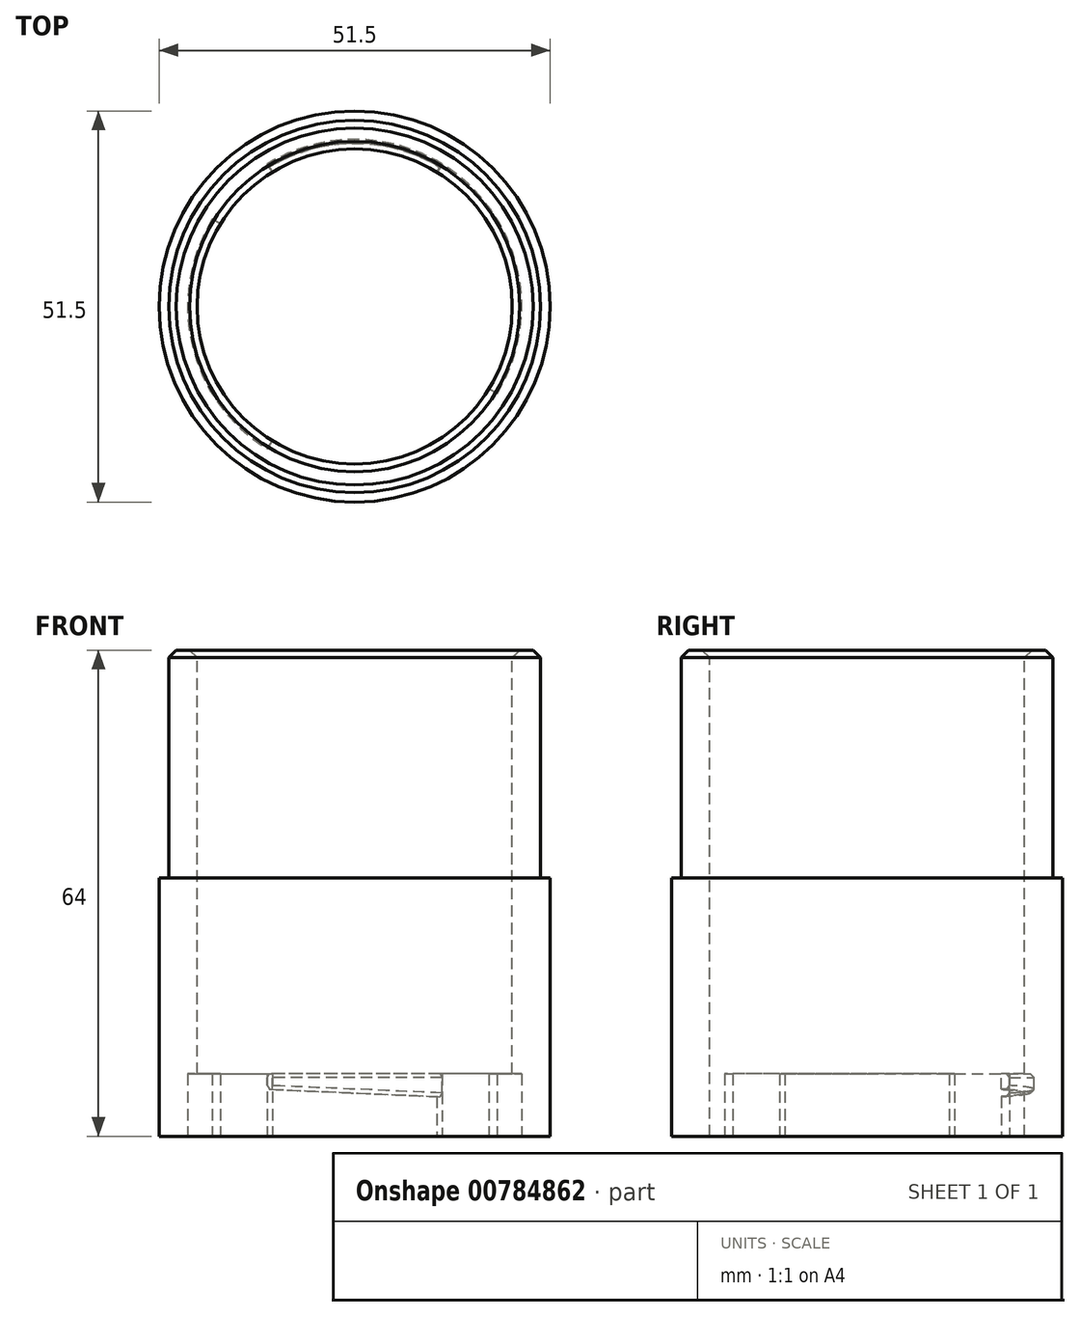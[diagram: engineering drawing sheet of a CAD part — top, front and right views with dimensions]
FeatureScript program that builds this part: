
annotation { "Feature Type Name" : "Feature", "Feature Type Description" : "" }
export const myFeature = defineFeature(function(context is Context, id is Id, definition is map)
    precondition{}
    {
        {
            var Q0;
            Q0=qCreatedBy(makeId("Top.planeOp"),FACE);
            var sketch = newSketch(context, id + "F0", { "sketchPlane" : qUnion([Q0])});
            skCircle(sketch, "E0", {"center": v(0, 0) * mm, "radius": 20.75 * mm});
            skCircle(sketch, "E1", {"center": v(0, 0) * mm, "radius": 18.75 * mm});
            skSolve(sketch);
        }
        {
            var Q0;
            Q0=makeQuery(id+"F0.imprint","IMPRINT",FACE,{"disambiguationData":[TD([[makeQuery(id+"F0.imprint","IMPRINT",EDGE,{"derivedFrom":sQuery(id+"F0.wireOp",EDGE,"E0")}),1.0]])]});
            extrude(context, id + "F1", {"entities" : qUnion([Q0]), "depth" : 34 * mm});
        }
        {
            var Q0;
            Q0=makeQuery(id+"F1.opExtrude","CAP_FACE",FACE,{"disambiguationData":[OSD([sQuery(id+"F0.wireOp",EDGE,"E0"),sQuery(id+"F0.wireOp",EDGE,"E1")])],"isStart":false});
            cPlane(context, id + "F2", {"entities" : qUnion([Q0]), "cplaneType" : CPlaneType.OFFSET, "offset" : 25.8 * mm, "oppositeDirection" : true, "width" : 150 * mm, "height" : 150 * mm});
        }
        {
            var Q0;
            Q0=qCreatedBy(id+"F2.planeOp",FACE);
            var sketch = newSketch(context, id + "F3", { "sketchPlane" : qUnion([Q0])});
            skCircle(sketch, "E2.0", {"center": v(0, 0) * mm, "radius": 20.75 * mm});
            skCircle(sketch, "E3", {"center": v(0, 0) * mm, "radius": 22 * mm});
            skLineSegment(sketch, "E4", {"start": v(-11.5, 18.75) * mm, "end": v(11.5, -18.75) * mm});
            skLineSegment(sketch, "E5", {"start": v(-11.5, -18.75) * mm, "end": v(11.5, 18.75) * mm});
            skLineSegment(sketch, "E6", {"start": v(-11.5, 18.75) * mm, "end": v(0, 21.22) * mm, "construction": true});
            skLineSegment(sketch, "E7", {"start": v(0, 21.22) * mm, "end": v(11.5, 18.75) * mm, "construction": true});
            skSolve(sketch);
        }
        {
            var Q0;
            {var subQ0=sQuery(id+"F3.wireOp",EDGE,"E4");var subQ1=sQuery(id+"F3.wireOp",EDGE,"E2.0");var subQ2=makeQuery(id+"F3.imprint","INTERSECT",VERTEX,{"disambiguationData":[OD(0.0)],"derivedFrom":[subQ1,subQ0]});Q0=makeQuery(id+"F3.imprint","IMPRINT",FACE,{"disambiguationData":[TD([[makeQuery(id+"F3.imprint","IMPRINT",EDGE,{"disambiguationData":[TD([[subQ2,1.0]])],"derivedFrom":subQ1}),-1.0]])]});}
            var Q1;
            {var subQ0=sQuery(id+"F3.wireOp",EDGE,"E5");var subQ1=sQuery(id+"F3.wireOp",EDGE,"E2.0");var subQ2=makeQuery(id+"F3.imprint","INTERSECT",VERTEX,{"disambiguationData":[OD(1.0)],"derivedFrom":[subQ1,subQ0]});Q1=makeQuery(id+"F3.imprint","IMPRINT",FACE,{"disambiguationData":[TD([[makeQuery(id+"F3.imprint","IMPRINT",EDGE,{"disambiguationData":[TD([[subQ2,-1.0]])],"derivedFrom":subQ1}),-1.0]])]});}
            extrude(context, id + "F4", {"entities" : qUnion([Q0, Q1]), "operationType" : NewBodyOperationType.ADD, "oppositeDirection" : true, "depth" : 3 * mm, "offsetDistance" : 25 * mm});
        }
        {
            var Q0;
            Q0=qCreatedBy(makeId("Front.planeOp"),FACE);
            cPlane(context, id + "F5", {"entities" : qUnion([Q0]), "cplaneType" : CPlaneType.OFFSET, "offset" : 25 * mm, "width" : 150 * mm, "height" : 150 * mm});
        }
        {
            var Q0;
            Q0=qCreatedBy(id+"F5.planeOp",FACE);
            var sketch = newSketch(context, id + "F6", { "sketchPlane" : qUnion([Q0])});
            skLineSegment(sketch, "E8.0.0", {"start": v(11.5, 8.2) * mm, "end": v(-11.5, 8.2) * mm});
            skLineSegment(sketch, "E8.0.1", {"start": v(-11.5, 8.2) * mm, "end": v(-11.5, 5.2) * mm});
            skLineSegment(sketch, "E8.0.2", {"start": v(-11.5, 5.2) * mm, "end": v(11.5, 5.2) * mm});
            skLineSegment(sketch, "E8.0.3", {"start": v(11.5, 5.2) * mm, "end": v(11.5, 8.2) * mm});
            skLineSegment(sketch, "E9", {"start": v(11.5, 6.2) * mm, "end": v(-11.5, 5.2) * mm});
            skSolve(sketch);
        }
        {
            var Q0;
            {var subQ0=sQuery(id+"F6.wireOp",EDGE,"E8.0.2");Q0=makeQuery(id+"F6.imprint","IMPRINT",FACE,{"disambiguationData":[TD([[makeQuery(id+"F6.imprint","IMPRINT",EDGE,{"derivedFrom":subQ0}),1.0]])]});}
            var Q1;
            Q1=makeQuery(id+"F1.opExtrude","SWEPT_FACE",FACE,{"disambiguationData":[OSD([sQuery(id+"F0.wireOp",EDGE,"E0")])]});
            extrude(context, id + "F7", {"entities" : qUnion([Q0]), "operationType" : NewBodyOperationType.REMOVE, "endBound" : BoundingType.UP_TO_SURFACE, "oppositeDirection" : true, "endBoundEntityFace" : qUnion([Q1]), "depth" : 25 * mm});
        }
        {
            var Q0;
            Q0=qCreatedBy(makeId("Front.planeOp"),FACE);
            cPlane(context, id + "F8", {"entities" : qUnion([Q0]), "cplaneType" : CPlaneType.OFFSET, "offset" : 25 * mm, "oppositeDirection" : true, "width" : 150 * mm, "height" : 150 * mm});
        }
        {
            var Q0;
            Q0=qCreatedBy(id+"F8.planeOp",FACE);
            var sketch = newSketch(context, id + "F9", { "sketchPlane" : qUnion([Q0])});
            skLineSegment(sketch, "E10.0.0", {"start": v(-11.5, 8.2) * mm, "end": v(11.5, 8.2) * mm});
            skLineSegment(sketch, "E10.0.1", {"start": v(11.5, 8.2) * mm, "end": v(11.5, 5.2) * mm});
            skLineSegment(sketch, "E10.0.2", {"start": v(11.5, 5.2) * mm, "end": v(-11.5, 5.2) * mm});
            skLineSegment(sketch, "E10.0.3", {"start": v(-11.5, 5.2) * mm, "end": v(-11.5, 8.2) * mm});
            skLineSegment(sketch, "E11", {"start": v(11.5, 5.2) * mm, "end": v(-11.5, 6.2) * mm});
            skSolve(sketch);
        }
        {
            var Q0;
            {var subQ0=sQuery(id+"F9.wireOp",EDGE,"E10.0.2");Q0=makeQuery(id+"F9.imprint","IMPRINT",FACE,{"disambiguationData":[TD([[makeQuery(id+"F9.imprint","IMPRINT",EDGE,{"derivedFrom":subQ0}),-1.0]])]});}
            var Q1;
            Q1=makeQuery(id+"F7.boolean.opBoolean","MERGE",FACE,{"derivedFrom":[makeQuery(id+"F1.opExtrude","SWEPT_FACE",FACE,{"disambiguationData":[OSD([sQuery(id+"F0.wireOp",EDGE,"E0")])]})],"fromTools":[makeQuery(id+"F7.opExtrude","CAP_FACE",FACE,{"disambiguationData":[OSD([sQuery(id+"F6.wireOp",EDGE,"E8.0.2"),sQuery(id+"F6.wireOp",EDGE,"E8.0.3"),sQuery(id+"F6.wireOp",EDGE,"E9")])],"isStart":false})]});
            extrude(context, id + "F10", {"entities" : qUnion([Q0]), "operationType" : NewBodyOperationType.REMOVE, "endBound" : BoundingType.UP_TO_SURFACE, "endBoundEntityFace" : qUnion([Q1]), "depth" : 25 * mm});
        }
        {
            var Q0;
            Q0=makeQuery(id+"F1.opExtrude","CAP_FACE",FACE,{"disambiguationData":[OSD([sQuery(id+"F0.wireOp",EDGE,"E0"),sQuery(id+"F0.wireOp",EDGE,"E1")])],"isStart":true});
            var sketch = newSketch(context, id + "F11", { "sketchPlane" : qUnion([Q0])});
            skCircle(sketch, "E12", {"center": v(0, 0) * mm, "radius": 24.25 * mm});
            skSolve(sketch);
        }
        {
            var Q0;
            Q0=makeQuery(id+"F11.imprint","IMPRINT",FACE,{"disambiguationData":[TD([[makeQuery(id+"F11.imprint","IMPRINT",EDGE,{"derivedFrom":sQuery(id+"F11.wireOp",EDGE,"E12")}),1.0]])]});
            var Q1;
            Q1=makeQuery(id+"F11.imprint","IMPRINT",FACE,{"disambiguationData":[TD([[makeQuery(id+"F11.imprint","IMPRINT",EDGE,{"derivedFrom":makeQuery(id+"F1.opExtrude","CAP_EDGE",EDGE,{"disambiguationData":[OSD([sQuery(id+"F0.wireOp",EDGE,"E0")])],"isStart":true})}),-1.0]])]});
            extrude(context, id + "F12", {"entities" : qUnion([Q0, Q1]), "operationType" : NewBodyOperationType.ADD, "depth" : 3 * mm});
        }
        {
            var Q0;
            Q0=makeQuery(id+"F12.opExtrude","CAP_FACE",FACE,{"disambiguationData":[OSD([sQuery(id+"F0.wireOp",EDGE,"E1"),sQuery(id+"F11.wireOp",EDGE,"E12")])],"isStart":false});
            var sketch = newSketch(context, id + "F13", { "sketchPlane" : qUnion([Q0])});
            skCircle(sketch, "E13.0", {"center": v(0, 0) * mm, "radius": 20.75 * mm});
            skCircle(sketch, "E14", {"center": v(0, 0) * mm, "radius": 16.75 * mm});
            skCircle(sketch, "E15.0", {"center": v(0, 0) * mm, "radius": 18.75 * mm});
            skSolve(sketch);
        }
        {
            var Q0;
            Q0=makeQuery(id+"F13.imprint","IMPRINT",FACE,{"disambiguationData":[TD([[makeQuery(id+"F13.imprint","IMPRINT",EDGE,{"derivedFrom":sQuery(id+"F13.wireOp",EDGE,"E14")}),-1.0]])]});
            extrude(context, id + "F14", {"entities" : qUnion([Q0]), "operationType" : NewBodyOperationType.ADD, "oppositeDirection" : true, "depth" : 3 * mm});
        }
        {
            var Q0;
            Q0=makeQuery(id+"F13.imprint","IMPRINT",FACE,{"disambiguationData":[TD([[makeQuery(id+"F13.imprint","IMPRINT",EDGE,{"derivedFrom":sQuery(id+"F13.wireOp",EDGE,"E13.0")}),1.0]])]});
            extrude(context, id + "F15", {"entities" : qUnion([Q0]), "operationType" : NewBodyOperationType.ADD, "depth" : 35 * mm});
        }
        {
            var Q0;
            Q0=makeQuery(id+"F1.opExtrude","CAP_EDGE",EDGE,{"disambiguationData":[OSD([sQuery(id+"F0.wireOp",EDGE,"E0")])],"isStart":false});
            var Q1;
            Q1=makeQuery(id+"F1.opExtrude","CAP_EDGE",EDGE,{"disambiguationData":[OSD([sQuery(id+"F0.wireOp",EDGE,"E1")])],"isStart":false});
            var Q2;
            {var subQ0=sQuery(id+"F3.wireOp",EDGE,"E3");Q2=makeQuery(id+"F4.opExtrude","CAP_EDGE",EDGE,{"disambiguationData":[OSD([subQ0]),TDD([makeQuery(id+"F3.imprint","IMPRINT",EDGE,{"disambiguationData":[TD([[makeQuery(id+"F3.imprint","INTERSECT",VERTEX,{"disambiguationData":[OD(1.0)],"derivedFrom":[subQ0,sQuery(id+"F3.wireOp",EDGE,"E4")]}),1.0]])],"derivedFrom":subQ0})])],"isStart":true});}
            var Q3;
            {var subQ0=sQuery(id+"F3.wireOp",EDGE,"E3");Q3=makeQuery(id+"F7.boolean.opBoolean","INTERSECT",EDGE,{"derivedFrom":[makeQuery(id+"F4.opExtrude","SWEPT_FACE",FACE,{"disambiguationData":[OSD([subQ0]),TDD([makeQuery(id+"F3.imprint","IMPRINT",EDGE,{"disambiguationData":[TD([[makeQuery(id+"F3.imprint","INTERSECT",VERTEX,{"disambiguationData":[OD(1.0)],"derivedFrom":[subQ0,sQuery(id+"F3.wireOp",EDGE,"E4")]}),1.0]])],"derivedFrom":subQ0})])]}),makeQuery(id+"F7.opExtrude","SWEPT_FACE",FACE,{"disambiguationData":[OSD([sQuery(id+"F6.wireOp",EDGE,"E9")])]})]});}
            var Q4;
            {var subQ0=sQuery(id+"F3.wireOp",EDGE,"E3");Q4=makeQuery(id+"F4.opExtrude","CAP_EDGE",EDGE,{"disambiguationData":[OSD([subQ0]),TDD([makeQuery(id+"F3.imprint","IMPRINT",EDGE,{"disambiguationData":[TD([[makeQuery(id+"F3.imprint","INTERSECT",VERTEX,{"disambiguationData":[OD(0.0)],"derivedFrom":[subQ0,sQuery(id+"F3.wireOp",EDGE,"E4")]}),1.0]])],"derivedFrom":subQ0})])],"isStart":true});}
            var Q5;
            {var subQ0=sQuery(id+"F3.wireOp",EDGE,"E3");Q5=makeQuery(id+"F10.boolean.opBoolean","INTERSECT",EDGE,{"derivedFrom":[makeQuery(id+"F4.opExtrude","SWEPT_FACE",FACE,{"disambiguationData":[OSD([subQ0]),TDD([makeQuery(id+"F3.imprint","IMPRINT",EDGE,{"disambiguationData":[TD([[makeQuery(id+"F3.imprint","INTERSECT",VERTEX,{"disambiguationData":[OD(0.0)],"derivedFrom":[subQ0,sQuery(id+"F3.wireOp",EDGE,"E4")]}),1.0]])],"derivedFrom":subQ0})])]}),makeQuery(id+"F10.opExtrude","SWEPT_FACE",FACE,{"disambiguationData":[OSD([sQuery(id+"F9.wireOp",EDGE,"E11")])]})]});}
            var Q6;
            Q6=makeQuery(id+"F1.opExtrude","CAP_EDGE",EDGE,{"disambiguationData":[OSD([sQuery(id+"F0.wireOp",EDGE,"E0")])],"isStart":true});
            chamfer(context, id + "F16", {"entities" : qUnion([Q0, Q1, Q2, Q3, Q4, Q5, Q6]), "width" : 0.5 * mm, "tangentPropagation" : true});
        }
        {
            var Q0;
            Q0=makeQuery(id+"F14.opExtrude","CAP_EDGE",EDGE,{"disambiguationData":[OSD([sQuery(id+"F13.wireOp",EDGE,"E14")])],"isStart":true});
            var Q1;
            Q1=makeQuery(id+"F14.opExtrude","CAP_EDGE",EDGE,{"disambiguationData":[OSD([sQuery(id+"F13.wireOp",EDGE,"E14")])],"isStart":false});
            var Q2;
            Q2=makeQuery(id+"F15.opExtrude","CAP_EDGE",EDGE,{"disambiguationData":[OSD([sQuery(id+"F13.wireOp",EDGE,"E13.0")])],"isStart":true});
            var Q3;
            Q3=makeQuery(id+"F12.opExtrude","CAP_EDGE",EDGE,{"disambiguationData":[OSD([sQuery(id+"F11.wireOp",EDGE,"E12")])],"isStart":false});
            var Q4;
            Q4=makeQuery(id+"F12.opExtrude","CAP_EDGE",EDGE,{"disambiguationData":[OSD([sQuery(id+"F11.wireOp",EDGE,"E12")])],"isStart":true});
            fillet(context, id + "F17", {"entities" : qUnion([Q0, Q1, Q2, Q3, Q4]), "radius" : 1.5 * mm, "tangentPropagation" : true, "allowEdgeOverflow" : false});
        }
        {
            var Q0;
            Q0=makeQuery(id+"F1.opExtrude","CAP_FACE",FACE,{"disambiguationData":[OSD([sQuery(id+"F0.wireOp",EDGE,"E0"),sQuery(id+"F0.wireOp",EDGE,"E1")])],"isStart":false});
            var sketch = newSketch(context, id + "F18", { "sketchPlane" : qUnion([Q0])});
            skCircle(sketch, "E16", {"center": v(0, 0) * mm, "radius": 24.75 * mm});
            skCircle(sketch, "E17.0", {"center": v(0, 0) * mm, "radius": 20.75 * mm});
            skSolve(sketch);
        }
        {
            var Q0;
            Q0=makeQuery(id+"F18.imprint","IMPRINT",FACE,{"disambiguationData":[TD([[makeQuery(id+"F18.imprint","IMPRINT",EDGE,{"derivedFrom":sQuery(id+"F18.wireOp",EDGE,"E16")}),1.0]])]});
            var Q1;
            Q1=makeQuery(id+"F12.opExtrude","CAP_FACE",FACE,{"disambiguationData":[OSD([sQuery(id+"F0.wireOp",EDGE,"E1"),sQuery(id+"F11.wireOp",EDGE,"E12")])],"isStart":true});
            extrude(context, id + "F19", {"entities" : qUnion([Q0]), "endBound" : BoundingType.UP_TO_SURFACE, "oppositeDirection" : true, "endBoundEntityFace" : qUnion([Q1]), "depth" : 35 * mm});
        }
        {
            var Q0;
            Q0=makeQuery(id+"F1.opExtrude","SWEPT_BODY",BODY,{"disambiguationData":[OSD([sQuery(id+"F0.wireOp",EDGE,"E0"),sQuery(id+"F0.wireOp",EDGE,"E1")])]});
            var Q1;
            Q1=makeQuery(id+"F19.opExtrude","SWEPT_BODY",BODY,{"disambiguationData":[OSD([sQuery(id+"F18.wireOp",EDGE,"E16"),sQuery(id+"F18.wireOp",EDGE,"E17.0")])]});
            booleanBodies(context, id + "F20", {"operationType" : BooleanOperationType.SUBTRACTION, "tools" : qUnion([Q0]), "targets" : qUnion([Q1])});
        }
        {
            var Q0;
            Q0=makeQuery(id+"F19.opExtrude","CAP_FACE",FACE,{"disambiguationData":[OSD([sQuery(id+"F18.wireOp",EDGE,"E16"),sQuery(id+"F18.wireOp",EDGE,"E17.0")])],"isStart":false});
            var sketch = newSketch(context, id + "F21", { "sketchPlane" : qUnion([Q0])});
            skLineSegment(sketch, "E18.0.0", {"start": v(-11.23, 18.32) * mm, "end": v(-10.85, 17.69) * mm});
            skLineSegment(sketch, "E18.0.2", {"start": v(-10.85, 17.69) * mm, "end": v(-11.24, 18.33) * mm});
            skLineSegment(sketch, "E18.0.3", {"start": v(-11.5, 18.75) * mm, "end": v(-11.24, 18.33) * mm});
            skFitSpline(sketch, "E18.0.5", {"points": [v(-11.5, 18.76) * mm, v(-11.41, 18.61) * mm, v(-11.32, 18.47) * mm, v(-11.23, 18.32) * mm]});
            skLineSegment(sketch, "E19.0.0", {"start": v(11.23, -18.32) * mm, "end": v(10.85, -17.69) * mm});
            skLineSegment(sketch, "E19.0.2", {"start": v(10.85, -17.69) * mm, "end": v(11.24, -18.33) * mm});
            skLineSegment(sketch, "E19.0.3", {"start": v(11.24, -18.33) * mm, "end": v(11.5, -18.75) * mm});
            skFitSpline(sketch, "E19.0.5", {"points": [v(11.5, -18.76) * mm, v(11.41, -18.61) * mm, v(11.32, -18.47) * mm, v(11.23, -18.32) * mm]});
            skCircle(sketch, "E20", {"center": v(0, 0) * mm, "radius": 20.75 * mm});
            skCircle(sketch, "E21", {"center": v(0, 0) * mm, "radius": 22 * mm});
            skLineSegment(sketch, "E22", {"start": v(18.76, 11.5) * mm, "end": v(0, 0) * mm});
            skLineSegment(sketch, "E23", {"start": v(0, 0) * mm, "end": v(-18.76, -11.5) * mm});
            skSolve(sketch);
        }
        {
            var Q0;
            {var subQ0=sQuery(id+"F21.wireOp",EDGE,"E19.0.5");var subQ3=makeQuery(id+"F21.imprint","IMPRINT",VERTEX,{"derivedFrom":subQ0});Q0=makeQuery(id+"F21.imprint","IMPRINT",FACE,{"disambiguationData":[TD([[makeQuery(id+"F21.imprint","IMPRINT",EDGE,{"disambiguationData":[TD([[subQ3,1.0]])],"derivedFrom":subQ0}),-1.0]])]});}
            var Q1;
            {var subQ0=sQuery(id+"F21.wireOp",EDGE,"E20");var subQ1=sQuery(id+"F21.wireOp",EDGE,"E19.0.2");var subQ2=makeQuery(id+"F21.imprint","INTERSECT",VERTEX,{"derivedFrom":[subQ1,subQ0]});Q1=makeQuery(id+"F21.imprint","IMPRINT",FACE,{"disambiguationData":[TD([[makeQuery(id+"F21.imprint","IMPRINT",EDGE,{"disambiguationData":[TD([[subQ2,-1.0]])],"derivedFrom":subQ0}),-1.0]])]});}
            var Q2;
            {var subQ1=sQuery(id+"F21.wireOp",EDGE,"E18.0.5");var subQ5=makeQuery(id+"F21.imprint","IMPRINT",VERTEX,{"derivedFrom":subQ1});Q2=makeQuery(id+"F21.imprint","IMPRINT",FACE,{"disambiguationData":[TD([[makeQuery(id+"F21.imprint","IMPRINT",EDGE,{"disambiguationData":[TD([[subQ5,1.0]])],"derivedFrom":subQ1}),-1.0]])]});}
            var Q3;
            {var subQ0=sQuery(id+"F21.wireOp",EDGE,"E20");var subQ1=sQuery(id+"F21.wireOp",EDGE,"E18.0.2");var subQ2=makeQuery(id+"F21.imprint","INTERSECT",VERTEX,{"derivedFrom":[subQ1,subQ0]});Q3=makeQuery(id+"F21.imprint","IMPRINT",FACE,{"disambiguationData":[TD([[makeQuery(id+"F21.imprint","IMPRINT",EDGE,{"disambiguationData":[TD([[subQ2,-1.0]])],"derivedFrom":subQ0}),-1.0]])]});}
            var Q4;
            {var subQ0=sQuery(id+"F3.wireOp",EDGE,"E5");var subQ1=sQuery(id+"F3.wireOp",EDGE,"E3");var subQ2=makeQuery(id+"F3.imprint","INTERSECT",VERTEX,{"disambiguationData":[OD(1.0)],"derivedFrom":[subQ1,subQ0]});var subQ3=sQuery(id+"F3.wireOp",EDGE,"E2.0");var subQ5=sQuery(id+"F3.wireOp",EDGE,"E4");var subQ6=makeQuery(id+"F3.imprint","INTERSECT",VERTEX,{"disambiguationData":[OD(0.0)],"derivedFrom":[subQ1,subQ5]});var subQ7=makeQuery(id+"F3.imprint","INTERSECT",VERTEX,{"disambiguationData":[OD(0.0)],"derivedFrom":[subQ3,subQ5]});Q4=makeQuery(id+"F20.opBoolean","COPY",FACE,{"derivedFrom":makeQuery(id+"F4.opExtrude","CAP_FACE",FACE,{"disambiguationData":[OSD([subQ3,subQ1,subQ5,subQ0]),TDD([makeQuery(id+"F3.imprint","IMPRINT",EDGE,{"disambiguationData":[TD([[subQ7,1.0]])],"derivedFrom":subQ3}),makeQuery(id+"F3.imprint","IMPRINT",EDGE,{"disambiguationData":[TD([[subQ6,1.0]])],"derivedFrom":subQ1}),makeQuery(id+"F3.imprint","IMPRINT",EDGE,{"disambiguationData":[TD([[subQ6,-1.0]])],"derivedFrom":subQ5}),makeQuery(id+"F3.imprint","IMPRINT",EDGE,{"disambiguationData":[TD([[subQ2,1.0]])],"derivedFrom":subQ0})])],"isStart":true})});}
            extrude(context, id + "F22", {"entities" : qUnion([Q0, Q1, Q2, Q3]), "operationType" : NewBodyOperationType.REMOVE, "endBound" : BoundingType.UP_TO_SURFACE, "oppositeDirection" : true, "endBoundEntityFace" : qUnion([Q4]), "depth" : 25 * mm, "offsetDistance" : 25 * mm});
        }
        {
            var Q0;
            Q0=makeQuery(id+"F19.opExtrude","CAP_FACE",FACE,{"disambiguationData":[OSD([sQuery(id+"F18.wireOp",EDGE,"E16"),sQuery(id+"F18.wireOp",EDGE,"E17.0")])],"isStart":true});
            var sketch = newSketch(context, id + "F23", { "sketchPlane" : qUnion([Q0])});
            skCircle(sketch, "E24.0", {"center": v(0, 0) * mm, "radius": 20.75 * mm});
            skCircle(sketch, "E25", {"center": v(0, 0) * mm, "radius": 24.5 * mm});
            skSolve(sketch);
        }
        {
            var Q0;
            Q0=makeQuery(id+"F23.imprint","IMPRINT",FACE,{"disambiguationData":[TD([[makeQuery(id+"F23.imprint","IMPRINT",EDGE,{"derivedFrom":sQuery(id+"F23.wireOp",EDGE,"E24.0")}),-1.0]])]});
            extrude(context, id + "F24", {"entities" : qUnion([Q0]), "operationType" : NewBodyOperationType.ADD, "depth" : 30 * mm, "offsetDistance" : 25 * mm});
        }
        {
            var Q0;
            Q0=makeQuery(id+"F19.opExtrude","CAP_FACE",FACE,{"disambiguationData":[OSD([sQuery(id+"F18.wireOp",EDGE,"E16"),sQuery(id+"F18.wireOp",EDGE,"E17.0")])],"isStart":false});
            var sketch = newSketch(context, id + "F25", { "sketchPlane" : qUnion([Q0])});
            skCircle(sketch, "E26.0", {"center": v(0, 0) * mm, "radius": 24.75 * mm});
            skCircle(sketch, "E27", {"center": v(0, 0) * mm, "radius": 25.75 * mm});
            skSolve(sketch);
        }
        {
            var Q0;
            Q0=makeQuery(id+"F25.imprint","IMPRINT",FACE,{"disambiguationData":[TD([[makeQuery(id+"F25.imprint","IMPRINT",EDGE,{"derivedFrom":sQuery(id+"F25.wireOp",EDGE,"E26.0")}),1.0]])]});
            var Q1;
            Q1=makeQuery(id+"F19.opExtrude","CAP_FACE",FACE,{"disambiguationData":[OSD([sQuery(id+"F18.wireOp",EDGE,"E16"),sQuery(id+"F18.wireOp",EDGE,"E17.0")])],"isStart":true});
            extrude(context, id + "F26", {"entities" : qUnion([Q0]), "operationType" : NewBodyOperationType.ADD, "endBound" : BoundingType.UP_TO_SURFACE, "oppositeDirection" : true, "depth" : 25 * mm, "endBoundEntityFace" : qUnion([Q1]), "offsetDistance" : 25 * mm});
        }
        {
            var Q0;
            Q0=makeQuery(id+"F24.opExtrude","CAP_EDGE",EDGE,{"disambiguationData":[OSD([sQuery(id+"F23.wireOp",EDGE,"E24.0")])],"isStart":false});
            var Q1;
            Q1=makeQuery(id+"F24.opExtrude","CAP_EDGE",EDGE,{"disambiguationData":[OSD([sQuery(id+"F23.wireOp",EDGE,"E25")])],"isStart":false});
            chamfer(context, id + "F27", {"entities" : qUnion([Q0, Q1]), "width" : 1 * mm, "tangentPropagation" : true});
        }
    });
